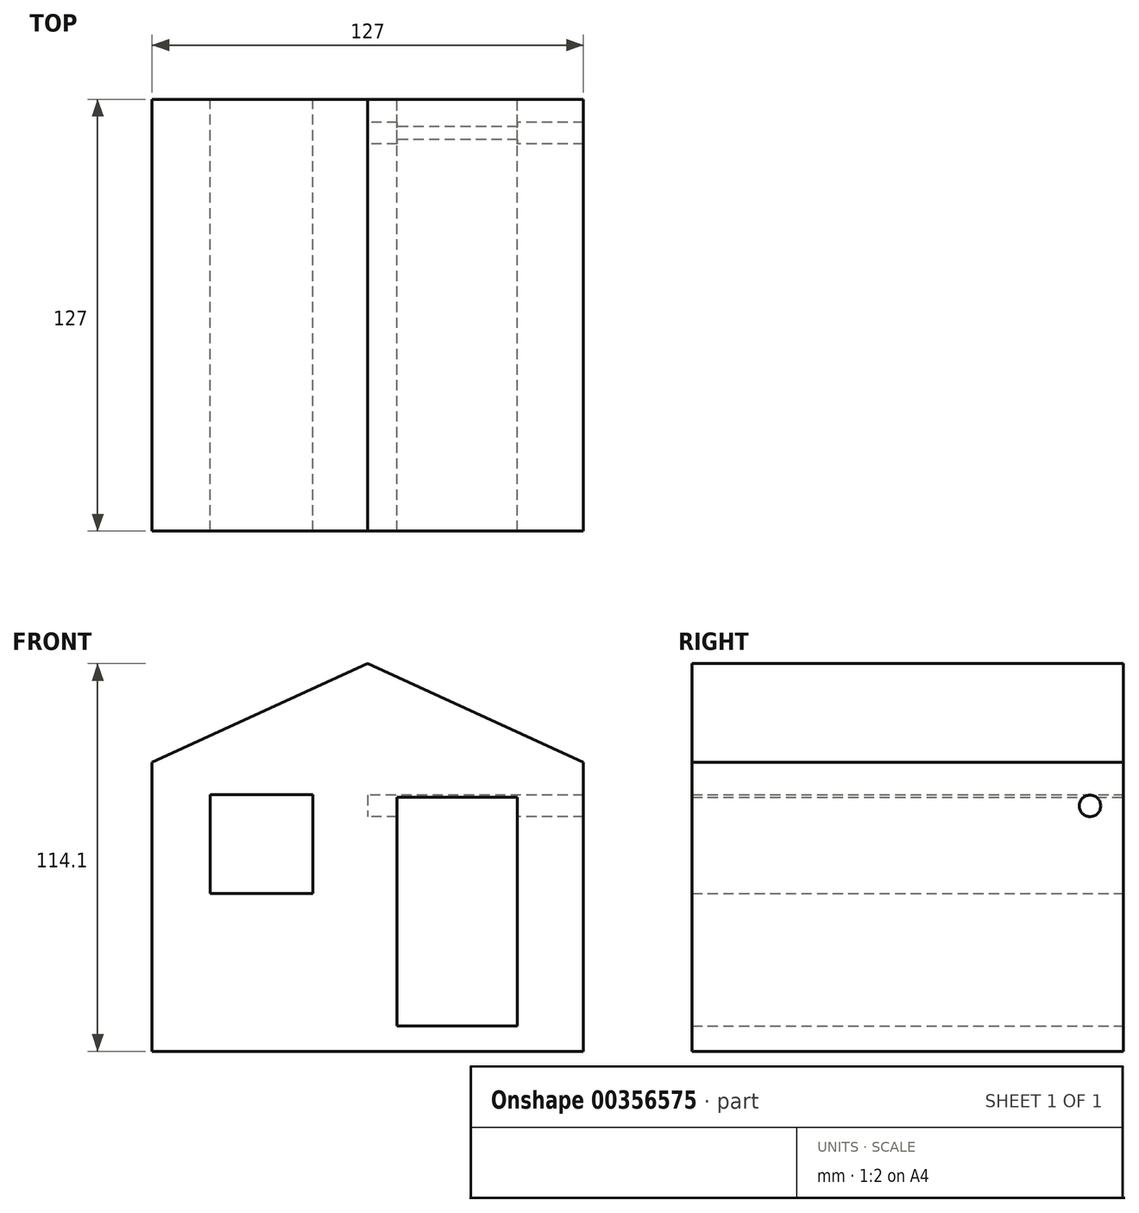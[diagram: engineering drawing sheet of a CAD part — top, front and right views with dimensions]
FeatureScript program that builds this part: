
annotation { "Feature Type Name" : "Feature", "Feature Type Description" : "" }
export const myFeature = defineFeature(function(context is Context, id is Id, definition is map)
    precondition{}
    {
        {
            var Q0;
            Q0=qCreatedBy(makeId("Front.planeOp"),FACE);
            var sketch = newSketch(context, id + "F0", { "sketchPlane" : qUnion([Q0])});
            skLineSegment(sketch, "E0.bottom", {"start": v(-63.5, 42.5) * mm, "end": v(63.5, 42.5) * mm});
            skLineSegment(sketch, "E0.top", {"start": v(-63.5, -42.5) * mm, "end": v(63.5, -42.5) * mm});
            skLineSegment(sketch, "E0.left", {"start": v(-63.5, 42.5) * mm, "end": v(-63.5, -42.5) * mm});
            skLineSegment(sketch, "E0.right", {"start": v(63.5, 42.5) * mm, "end": v(63.5, -42.5) * mm});
            skPoint(sketch, "E0.middle", {"position": v(0, 0) * mm});
            skLineSegment(sketch, "E1", {"start": v(-63.5, 42.5) * mm, "end": v(0, 71.6) * mm});
            skLineSegment(sketch, "E2", {"start": v(0, 71.6) * mm, "end": v(63.5, 42.5) * mm});
            skLineSegment(sketch, "E3.bottom", {"start": v(-46.43, 33.05) * mm, "end": v(-16.13, 33.05) * mm});
            skLineSegment(sketch, "E3.top", {"start": v(-46.43, 3.93) * mm, "end": v(-16.13, 3.93) * mm});
            skLineSegment(sketch, "E3.left", {"start": v(-46.43, 33.05) * mm, "end": v(-46.43, 3.93) * mm});
            skLineSegment(sketch, "E3.right", {"start": v(-16.13, 33.05) * mm, "end": v(-16.13, 3.93) * mm});
            skLineSegment(sketch, "E4.bottom", {"start": v(8.66, 32.26) * mm, "end": v(44.07, 32.26) * mm});
            skLineSegment(sketch, "E4.top", {"start": v(8.66, -35.02) * mm, "end": v(44.07, -35.02) * mm});
            skLineSegment(sketch, "E4.left", {"start": v(8.66, 32.26) * mm, "end": v(8.66, -35.02) * mm});
            skLineSegment(sketch, "E4.right", {"start": v(44.07, 32.26) * mm, "end": v(44.07, -35.02) * mm});
            skCircle(sketch, "E5", {"center": v(13.38, 0) * mm, "radius": 4.72 * mm});
            skSolve(sketch);
        }
        {
            var Q0;
            Q0=makeQuery(id+"F0.imprint","IMPRINT",FACE,{"disambiguationData":[TD([[makeQuery(id+"F0.imprint","IMPRINT",EDGE,{"derivedFrom":sQuery(id+"F0.wireOp",EDGE,"E0.bottom")}),-1.0]])]});
            var Q1;
            Q1=makeQuery(id+"F0.imprint","IMPRINT",FACE,{"disambiguationData":[TD([[makeQuery(id+"F0.imprint","IMPRINT",EDGE,{"derivedFrom":sQuery(id+"F0.wireOp",EDGE,"E0.bottom")}),1.0]])]});
            extrude(context, id + "F1", {"entities" : qUnion([Q0, Q1]), "depth" : 127 * mm});
        }
        {
            var Q0;
            Q0=qCreatedBy(makeId("Right.planeOp"),FACE);
            var sketch = newSketch(context, id + "F2", { "sketchPlane" : qUnion([Q0])});
            skLineSegment(sketch, "E6.bottom", {"start": v(-9.85, 29.72) * mm, "end": v(-51, 29.72) * mm});
            skLineSegment(sketch, "E6.top", {"start": v(-9.85, 0) * mm, "end": v(-51, 0) * mm});
            skLineSegment(sketch, "E6.left", {"start": v(-9.85, 29.72) * mm, "end": v(-9.85, 0) * mm});
            skLineSegment(sketch, "E6.right", {"start": v(-51, 29.72) * mm, "end": v(-51, 0) * mm});
            skLineSegment(sketch, "E7.bottom", {"start": v(-65.99, 29.97) * mm, "end": v(-115, 29.97) * mm});
            skLineSegment(sketch, "E7.top", {"start": v(-65.99, 0) * mm, "end": v(-115, 0) * mm});
            skLineSegment(sketch, "E7.left", {"start": v(-65.99, 29.97) * mm, "end": v(-65.99, 0) * mm});
            skLineSegment(sketch, "E7.right", {"start": v(-115, 29.97) * mm, "end": v(-115, 0) * mm});
            skSolve(sketch);
        }
        {
            var Q0;
            Q0=sQuery(id+"F2.wireOp",VERTEX,"E6.bottom.start");
            var Q1;
            Q1=makeQuery(id+"F1.opExtrude","SWEPT_BODY",BODY,{"disambiguationData":[OSD([sQuery(id+"F0.wireOp",EDGE,"E0.top"),sQuery(id+"F0.wireOp",EDGE,"E0.left"),sQuery(id+"F0.wireOp",EDGE,"E0.right"),sQuery(id+"F0.wireOp",EDGE,"E1"),sQuery(id+"F0.wireOp",EDGE,"E2"),sQuery(id+"F0.wireOp",EDGE,"E3.bottom"),sQuery(id+"F0.wireOp",EDGE,"E3.top"),sQuery(id+"F0.wireOp",EDGE,"E3.left"),sQuery(id+"F0.wireOp",EDGE,"E3.right"),sQuery(id+"F0.wireOp",EDGE,"E4.bottom"),sQuery(id+"F0.wireOp",EDGE,"E4.top"),sQuery(id+"F0.wireOp",EDGE,"E4.left"),sQuery(id+"F0.wireOp",EDGE,"E4.right")])]});
            hole(context, id + "F3", {"style" : HoleStyle.SIMPLE, "endStyle" : HoleEndStyle.THROUGH, "oppositeDirection" : true, "holeDiameter" : 6.35 * mm, "isTappedThrough" : true, "tappedDepth" : 12.7 * mm, "tapClearance" : 3, "locations" : qUnion([Q0]), "scope" : qUnion([Q1])});
        }
    });
